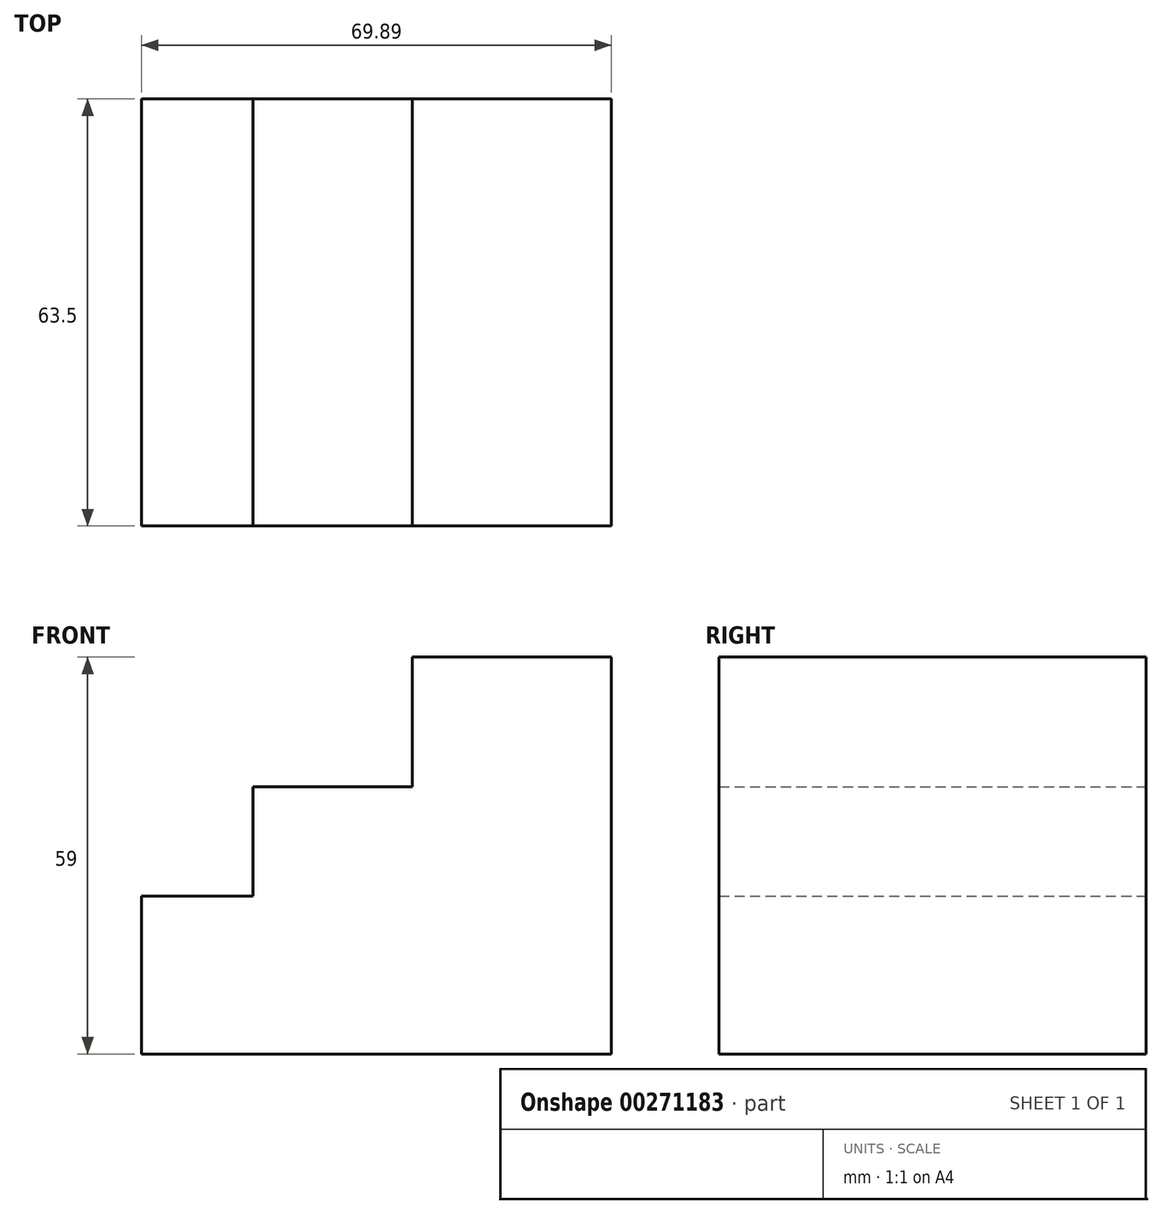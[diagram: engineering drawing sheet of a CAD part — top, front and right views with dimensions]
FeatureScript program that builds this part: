
annotation { "Feature Type Name" : "Feature", "Feature Type Description" : "" }
export const myFeature = defineFeature(function(context is Context, id is Id, definition is map)
    precondition{}
    {
        {
            var Q0;
            Q0=qCreatedBy(makeId("Front.planeOp"),FACE);
            var sketch = newSketch(context, id + "F0", { "sketchPlane" : qUnion([Q0])});
            skLineSegment(sketch, "E0.bottom", {"start": v(0, 0) * mm, "end": v(-29.6, 0) * mm});
            skLineSegment(sketch, "E0.top", {"start": v(0, 59) * mm, "end": v(-29.6, 59) * mm});
            skLineSegment(sketch, "E0.left", {"start": v(0, 0) * mm, "end": v(0, 59) * mm});
            skLineSegment(sketch, "E0.right", {"start": v(-29.6, 0) * mm, "end": v(-29.6, 59) * mm});
            skLineSegment(sketch, "E1", {"start": v(-29.6, 0) * mm, "end": v(-69.89, 0) * mm});
            skLineSegment(sketch, "E2", {"start": v(-69.89, 0) * mm, "end": v(-69.89, 23.49) * mm});
            skLineSegment(sketch, "E3", {"start": v(-69.89, 23.49) * mm, "end": v(-53.28, 23.49) * mm});
            skLineSegment(sketch, "E4", {"start": v(-53.28, 23.49) * mm, "end": v(-53.28, 39.72) * mm});
            skLineSegment(sketch, "E5", {"start": v(-53.28, 39.72) * mm, "end": v(-29.6, 39.72) * mm});
            skSolve(sketch);
        }
        {
            var Q0;
            Q0 = qSketchRegion(id + "F0", true);
            extrude(context, id + "F1", {"entities" : qUnion([Q0]), "depth" : 63.5 * mm});
        }
    });
